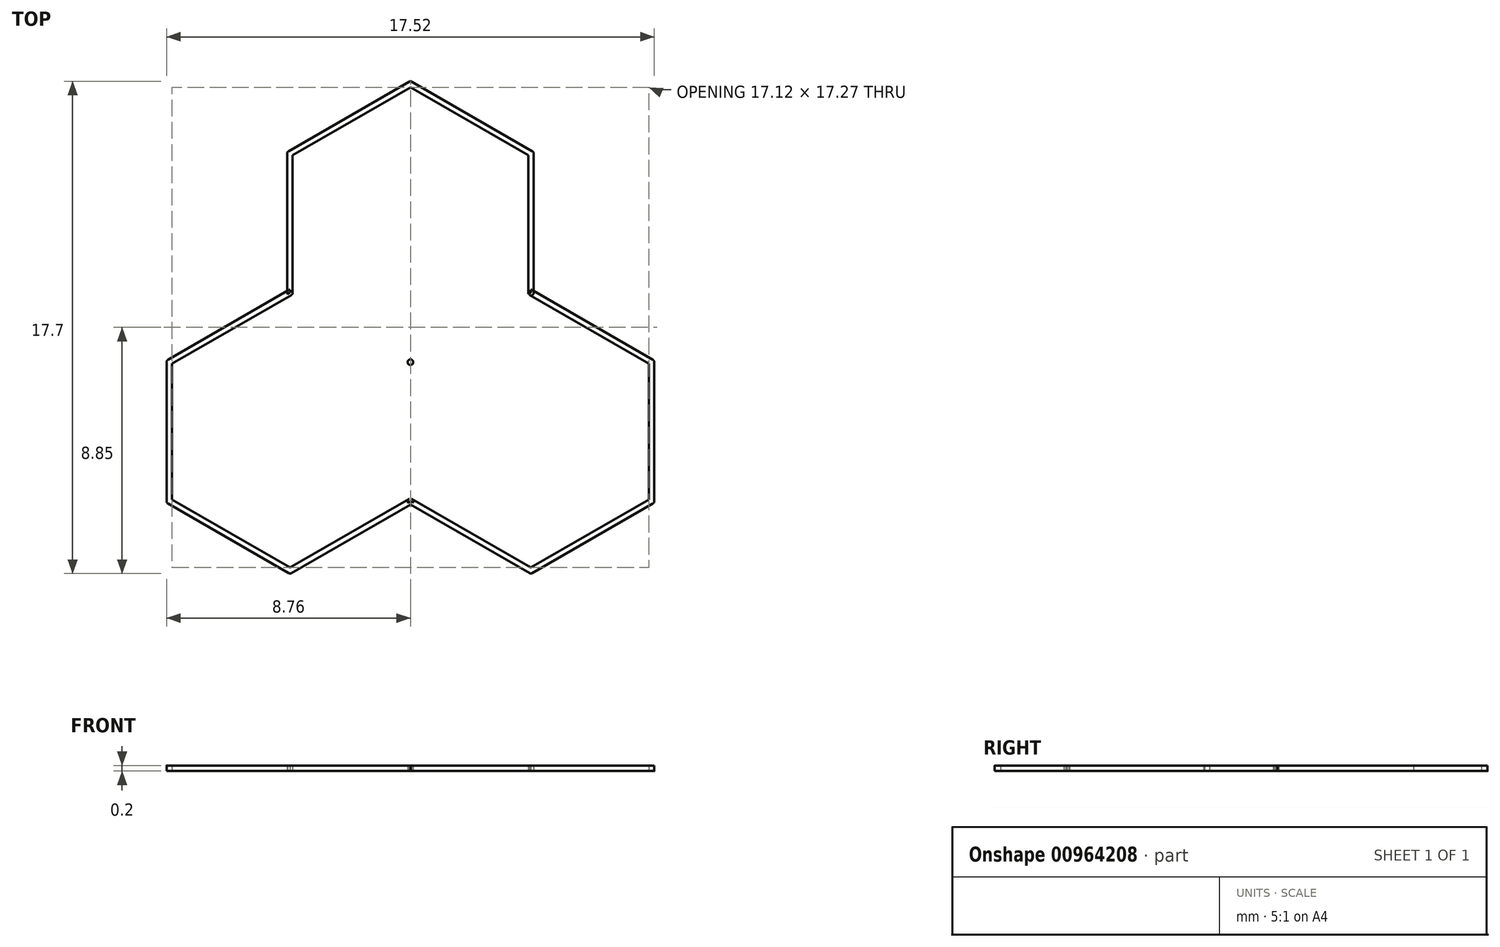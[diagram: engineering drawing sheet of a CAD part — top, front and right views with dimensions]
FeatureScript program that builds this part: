
annotation { "Feature Type Name" : "Feature", "Feature Type Description" : "" }
export const myFeature = defineFeature(function(context is Context, id is Id, definition is map)
    precondition{}
    {
        {
            var Q0;
            Q0=qCreatedBy(makeId("Top.planeOp"),FACE);
            var sketch = newSketch(context, id + "F0", { "sketchPlane" : qUnion([Q0])});
            skLineSegment(sketch, "E0.0", {"start": v(0, 5) * mm, "end": v(4.33, 2.5) * mm});
            skLineSegment(sketch, "E0.1", {"start": v(4.33, 2.5) * mm, "end": v(4.33, -2.5) * mm});
            skLineSegment(sketch, "E0.2", {"start": v(4.33, -2.5) * mm, "end": v(0, -5) * mm});
            skLineSegment(sketch, "E0.3", {"start": v(0, -5) * mm, "end": v(-4.33, -2.5) * mm});
            skLineSegment(sketch, "E0.4", {"start": v(-4.33, -2.5) * mm, "end": v(-4.33, 2.5) * mm});
            skLineSegment(sketch, "E0.5", {"start": v(-4.33, 2.5) * mm, "end": v(0, 5) * mm});
            skLineSegment(sketch, "E1", {"start": v(4.33, -2.5) * mm, "end": v(8.66, -5) * mm});
            skLineSegment(sketch, "E2", {"start": v(8.66, -5) * mm, "end": v(8.66, -10) * mm});
            skLineSegment(sketch, "E3", {"start": v(8.66, -10) * mm, "end": v(4.33, -12.5) * mm});
            skLineSegment(sketch, "E4", {"start": v(4.33, -12.5) * mm, "end": v(0, -10) * mm});
            skLineSegment(sketch, "E5", {"start": v(0, -10) * mm, "end": v(0, -5) * mm});
            skLineSegment(sketch, "E6", {"start": v(0, -10) * mm, "end": v(-4.33, -12.5) * mm});
            skLineSegment(sketch, "E7", {"start": v(-4.33, -12.5) * mm, "end": v(-8.66, -10) * mm});
            skLineSegment(sketch, "E8", {"start": v(-8.66, -10) * mm, "end": v(-8.66, -5) * mm});
            skLineSegment(sketch, "E9", {"start": v(-8.66, -5) * mm, "end": v(-4.33, -2.5) * mm});
            skArc(sketch, "E10.0.startCap", {"start": v(8.61, -9.91) * mm, "mid": v(8.75, -9.95) * mm, "end": v(8.71, -10.09) * mm});
            skArc(sketch, "E10.0.endCap", {"start": v(4.38, -12.59) * mm, "mid": v(4.24, -12.55) * mm, "end": v(4.28, -12.41) * mm});
            skLineSegment(sketch, "E10.0.left", {"start": v(8.71, -10.09) * mm, "end": v(4.38, -12.59) * mm});
            skLineSegment(sketch, "E10.0.right", {"start": v(8.61, -9.91) * mm, "end": v(4.28, -12.41) * mm});
            skArc(sketch, "E10.1.startCap", {"start": v(4.28, -2.59) * mm, "mid": v(4.24, -2.45) * mm, "end": v(4.38, -2.41) * mm});
            skArc(sketch, "E10.1.endCap", {"start": v(8.71, -4.91) * mm, "mid": v(8.75, -5.05) * mm, "end": v(8.61, -5.09) * mm});
            skLineSegment(sketch, "E10.1.left", {"start": v(4.38, -2.41) * mm, "end": v(8.71, -4.91) * mm});
            skLineSegment(sketch, "E10.1.right", {"start": v(4.28, -2.59) * mm, "end": v(8.61, -5.09) * mm});
            skArc(sketch, "E10.2.startCap", {"start": v(8.56, -5) * mm, "mid": v(8.66, -4.9) * mm, "end": v(8.76, -5) * mm});
            skArc(sketch, "E10.2.endCap", {"start": v(8.76, -10) * mm, "mid": v(8.66, -10.1) * mm, "end": v(8.56, -10) * mm});
            skLineSegment(sketch, "E10.2.left", {"start": v(8.76, -5) * mm, "end": v(8.76, -10) * mm});
            skLineSegment(sketch, "E10.2.right", {"start": v(8.56, -5) * mm, "end": v(8.56, -10) * mm});
            skArc(sketch, "E10.3.startCap", {"start": v(-4.28, -12.41) * mm, "mid": v(-4.24, -12.55) * mm, "end": v(-4.38, -12.59) * mm});
            skArc(sketch, "E10.3.endCap", {"start": v(-8.71, -10.09) * mm, "mid": v(-8.75, -9.95) * mm, "end": v(-8.61, -9.91) * mm});
            skLineSegment(sketch, "E10.3.left", {"start": v(-4.38, -12.59) * mm, "end": v(-8.71, -10.09) * mm});
            skLineSegment(sketch, "E10.3.right", {"start": v(-4.28, -12.41) * mm, "end": v(-8.61, -9.91) * mm});
            skArc(sketch, "E10.4.startCap", {"start": v(4.23, 2.5) * mm, "mid": v(4.33, 2.6) * mm, "end": v(4.43, 2.5) * mm});
            skArc(sketch, "E10.4.endCap", {"start": v(4.43, -2.5) * mm, "mid": v(4.33, -2.6) * mm, "end": v(4.23, -2.5) * mm});
            skLineSegment(sketch, "E10.4.left", {"start": v(4.43, 2.5) * mm, "end": v(4.43, -2.5) * mm});
            skLineSegment(sketch, "E10.4.right", {"start": v(4.23, 2.5) * mm, "end": v(4.23, -2.5) * mm});
            skArc(sketch, "E10.5.startCap", {"start": v(-4.28, 2.41) * mm, "mid": v(-4.42, 2.45) * mm, "end": v(-4.38, 2.59) * mm});
            skArc(sketch, "E10.5.endCap", {"start": v(-0.05, 5.09) * mm, "mid": v(0.09, 5.05) * mm, "end": v(0.05, 4.91) * mm});
            skLineSegment(sketch, "E10.5.left", {"start": v(-4.38, 2.59) * mm, "end": v(-0.05, 5.09) * mm});
            skLineSegment(sketch, "E10.5.right", {"start": v(-4.28, 2.41) * mm, "end": v(0.05, 4.91) * mm});
            skArc(sketch, "E10.6.startCap", {"start": v(0.1, -10) * mm, "mid": v(0, -10.1) * mm, "end": v(-0.1, -10) * mm});
            skArc(sketch, "E10.6.endCap", {"start": v(-0.1, -5) * mm, "mid": v(0, -4.9) * mm, "end": v(0.1, -5) * mm});
            skLineSegment(sketch, "E10.6.left", {"start": v(-0.1, -10) * mm, "end": v(-0.1, -5) * mm});
            skLineSegment(sketch, "E10.6.right", {"start": v(0.1, -10) * mm, "end": v(0.1, -5) * mm});
            skArc(sketch, "E10.7.startCap", {"start": v(4.28, -2.41) * mm, "mid": v(4.42, -2.45) * mm, "end": v(4.38, -2.59) * mm});
            skArc(sketch, "E10.7.endCap", {"start": v(0.05, -5.09) * mm, "mid": v(-0.09, -5.05) * mm, "end": v(-0.05, -4.91) * mm});
            skLineSegment(sketch, "E10.7.left", {"start": v(4.38, -2.59) * mm, "end": v(0.05, -5.09) * mm});
            skLineSegment(sketch, "E10.7.right", {"start": v(4.28, -2.41) * mm, "end": v(-0.05, -4.91) * mm});
            skArc(sketch, "E10.8.startCap", {"start": v(4.38, -12.41) * mm, "mid": v(4.42, -12.55) * mm, "end": v(4.28, -12.59) * mm});
            skArc(sketch, "E10.8.endCap", {"start": v(-0.05, -10.09) * mm, "mid": v(-0.09, -9.95) * mm, "end": v(0.05, -9.91) * mm});
            skLineSegment(sketch, "E10.8.left", {"start": v(4.28, -12.59) * mm, "end": v(-0.05, -10.09) * mm});
            skLineSegment(sketch, "E10.8.right", {"start": v(4.38, -12.41) * mm, "end": v(0.05, -9.91) * mm});
            skArc(sketch, "E10.9.startCap", {"start": v(-4.23, -2.5) * mm, "mid": v(-4.33, -2.6) * mm, "end": v(-4.43, -2.5) * mm});
            skArc(sketch, "E10.9.endCap", {"start": v(-4.43, 2.5) * mm, "mid": v(-4.33, 2.6) * mm, "end": v(-4.23, 2.5) * mm});
            skLineSegment(sketch, "E10.9.left", {"start": v(-4.43, -2.5) * mm, "end": v(-4.43, 2.5) * mm});
            skLineSegment(sketch, "E10.9.right", {"start": v(-4.23, -2.5) * mm, "end": v(-4.23, 2.5) * mm});
            skArc(sketch, "E10.10.startCap", {"start": v(-8.56, -10) * mm, "mid": v(-8.66, -10.1) * mm, "end": v(-8.76, -10) * mm});
            skArc(sketch, "E10.10.endCap", {"start": v(-8.76, -5) * mm, "mid": v(-8.66, -4.9) * mm, "end": v(-8.56, -5) * mm});
            skLineSegment(sketch, "E10.10.left", {"start": v(-8.76, -10) * mm, "end": v(-8.76, -5) * mm});
            skLineSegment(sketch, "E10.10.right", {"start": v(-8.56, -10) * mm, "end": v(-8.56, -5) * mm});
            skArc(sketch, "E10.11.startCap", {"start": v(-0.05, -9.91) * mm, "mid": v(0.09, -9.95) * mm, "end": v(0.05, -10.09) * mm});
            skArc(sketch, "E10.11.endCap", {"start": v(-4.28, -12.59) * mm, "mid": v(-4.42, -12.55) * mm, "end": v(-4.38, -12.41) * mm});
            skLineSegment(sketch, "E10.11.left", {"start": v(0.05, -10.09) * mm, "end": v(-4.28, -12.59) * mm});
            skLineSegment(sketch, "E10.11.right", {"start": v(-0.05, -9.91) * mm, "end": v(-4.38, -12.41) * mm});
            skArc(sketch, "E10.12.startCap", {"start": v(-8.61, -5.09) * mm, "mid": v(-8.75, -5.05) * mm, "end": v(-8.71, -4.91) * mm});
            skArc(sketch, "E10.12.endCap", {"start": v(-4.38, -2.41) * mm, "mid": v(-4.24, -2.45) * mm, "end": v(-4.28, -2.59) * mm});
            skLineSegment(sketch, "E10.12.left", {"start": v(-8.71, -4.91) * mm, "end": v(-4.38, -2.41) * mm});
            skLineSegment(sketch, "E10.12.right", {"start": v(-8.61, -5.09) * mm, "end": v(-4.28, -2.59) * mm});
            skArc(sketch, "E10.13.startCap", {"start": v(0.05, -4.91) * mm, "mid": v(0.09, -5.05) * mm, "end": v(-0.05, -5.09) * mm});
            skArc(sketch, "E10.13.endCap", {"start": v(-4.38, -2.59) * mm, "mid": v(-4.42, -2.45) * mm, "end": v(-4.28, -2.41) * mm});
            skLineSegment(sketch, "E10.13.left", {"start": v(-0.05, -5.09) * mm, "end": v(-4.38, -2.59) * mm});
            skLineSegment(sketch, "E10.13.right", {"start": v(0.05, -4.91) * mm, "end": v(-4.28, -2.41) * mm});
            skArc(sketch, "E10.14.startCap", {"start": v(-0.05, 4.91) * mm, "mid": v(-0.09, 5.05) * mm, "end": v(0.05, 5.09) * mm});
            skArc(sketch, "E10.14.endCap", {"start": v(4.38, 2.59) * mm, "mid": v(4.42, 2.45) * mm, "end": v(4.28, 2.41) * mm});
            skLineSegment(sketch, "E10.14.left", {"start": v(0.05, 5.09) * mm, "end": v(4.38, 2.59) * mm});
            skLineSegment(sketch, "E10.14.right", {"start": v(-0.05, 4.91) * mm, "end": v(4.28, 2.41) * mm});
            skSolve(sketch);
        }
        {
            var Q0;
            {var subQ5=sQuery(id+"F0.wireOp",EDGE,"E10.5.left");Q0=makeQuery(id+"F0.imprint","IMPRINT",FACE,{"disambiguationData":[TD([[makeQuery(id+"F0.imprint","IMPRINT",EDGE,{"derivedFrom":subQ5}),-1.0]])]});}
            var Q1;
            {var subQ4=sQuery(id+"F0.wireOp",EDGE,"E0.4");var subQ6=sQuery(id+"F0.wireOp",EDGE,"E0.5");var subQ7=makeQuery(id+"F0.imprint","INTERSECT",VERTEX,{"derivedFrom":[subQ4,subQ6]});Q1=makeQuery(id+"F0.imprint","IMPRINT",FACE,{"disambiguationData":[TD([[makeQuery(id+"F0.imprint","IMPRINT",EDGE,{"disambiguationData":[TD([[subQ7,1.0]])],"derivedFrom":subQ4}),1.0]])]});}
            var Q2;
            {var subQ0=sQuery(id+"F0.wireOp",EDGE,"E0.5");var subQ1=sQuery(id+"F0.wireOp",EDGE,"E0.4");var subQ2=makeQuery(id+"F0.imprint","INTERSECT",VERTEX,{"derivedFrom":[subQ1,subQ0]});Q2=makeQuery(id+"F0.imprint","IMPRINT",FACE,{"disambiguationData":[TD([[makeQuery(id+"F0.imprint","IMPRINT",EDGE,{"disambiguationData":[TD([[subQ2,1.0]])],"derivedFrom":subQ1}),-1.0]])]});}
            var Q3;
            {var subQ5=sQuery(id+"F0.wireOp",EDGE,"E10.13.endCap");var subQ7=sQuery(id+"F0.wireOp",EDGE,"E0.4");var subQ9=makeQuery(id+"F0.imprint","INTERSECT",VERTEX,{"derivedFrom":[subQ7,subQ5]});Q3=makeQuery(id+"F0.imprint","IMPRINT",FACE,{"disambiguationData":[TD([[makeQuery(id+"F0.imprint","IMPRINT",EDGE,{"disambiguationData":[TD([[subQ9,-1.0]])],"derivedFrom":subQ7}),1.0]])]});}
            var Q4;
            {var subQ5=sQuery(id+"F0.wireOp",EDGE,"E10.13.endCap");var subQ7=sQuery(id+"F0.wireOp",EDGE,"E0.4");var subQ8=makeQuery(id+"F0.imprint","INTERSECT",VERTEX,{"derivedFrom":[subQ7,subQ5]});Q4=makeQuery(id+"F0.imprint","IMPRINT",FACE,{"disambiguationData":[TD([[makeQuery(id+"F0.imprint","IMPRINT",EDGE,{"disambiguationData":[TD([[subQ8,-1.0]])],"derivedFrom":subQ7}),-1.0]])]});}
            var Q5;
            {var subQ1=sQuery(id+"F0.wireOp",EDGE,"E10.9.endCap");var subQ5=sQuery(id+"F0.wireOp",EDGE,"E0.5");var subQ6=makeQuery(id+"F0.imprint","INTERSECT",VERTEX,{"derivedFrom":[subQ5,subQ1]});Q5=makeQuery(id+"F0.imprint","IMPRINT",FACE,{"disambiguationData":[TD([[makeQuery(id+"F0.imprint","IMPRINT",EDGE,{"disambiguationData":[TD([[subQ6,-1.0]])],"derivedFrom":subQ5}),-1.0]])]});}
            var Q6;
            {var subQ7=sQuery(id+"F0.wireOp",EDGE,"E0.0");var subQ9=sQuery(id+"F0.wireOp",EDGE,"E0.5");var subQ10=makeQuery(id+"F0.imprint","INTERSECT",VERTEX,{"derivedFrom":[subQ7,subQ9]});Q6=makeQuery(id+"F0.imprint","IMPRINT",FACE,{"disambiguationData":[TD([[makeQuery(id+"F0.imprint","IMPRINT",EDGE,{"disambiguationData":[TD([[subQ10,-1.0]])],"derivedFrom":subQ7}),-1.0]])]});}
            var Q7;
            {var subQ2=sQuery(id+"F0.wireOp",EDGE,"E0.5");var subQ6=sQuery(id+"F0.wireOp",EDGE,"E0.0");var subQ8=makeQuery(id+"F0.imprint","INTERSECT",VERTEX,{"derivedFrom":[subQ6,subQ2]});Q7=makeQuery(id+"F0.imprint","IMPRINT",FACE,{"disambiguationData":[TD([[makeQuery(id+"F0.imprint","IMPRINT",EDGE,{"disambiguationData":[TD([[subQ8,-1.0]])],"derivedFrom":subQ6}),1.0]])]});}
            var Q8;
            {var subQ5=sQuery(id+"F0.wireOp",EDGE,"E10.14.left");Q8=makeQuery(id+"F0.imprint","IMPRINT",FACE,{"disambiguationData":[TD([[makeQuery(id+"F0.imprint","IMPRINT",EDGE,{"derivedFrom":subQ5}),-1.0]])]});}
            var Q9;
            {var subQ1=sQuery(id+"F0.wireOp",EDGE,"E10.5.endCap");var subQ3=sQuery(id+"F0.wireOp",EDGE,"E0.0");var subQ4=makeQuery(id+"F0.imprint","INTERSECT",VERTEX,{"derivedFrom":[subQ3,subQ1]});Q9=makeQuery(id+"F0.imprint","IMPRINT",FACE,{"disambiguationData":[TD([[makeQuery(id+"F0.imprint","IMPRINT",EDGE,{"disambiguationData":[TD([[subQ4,-1.0]])],"derivedFrom":subQ3}),-1.0]])]});}
            var Q10;
            {var subQ5=sQuery(id+"F0.wireOp",EDGE,"E0.0");var subQ7=sQuery(id+"F0.wireOp",EDGE,"E0.1");var subQ8=makeQuery(id+"F0.imprint","INTERSECT",VERTEX,{"derivedFrom":[subQ5,subQ7]});Q10=makeQuery(id+"F0.imprint","IMPRINT",FACE,{"disambiguationData":[TD([[makeQuery(id+"F0.imprint","IMPRINT",EDGE,{"disambiguationData":[TD([[subQ8,1.0]])],"derivedFrom":subQ5}),-1.0]])]});}
            var Q11;
            {var subQ4=sQuery(id+"F0.wireOp",EDGE,"E0.0");var subQ6=sQuery(id+"F0.wireOp",EDGE,"E0.1");var subQ7=makeQuery(id+"F0.imprint","INTERSECT",VERTEX,{"derivedFrom":[subQ4,subQ6]});Q11=makeQuery(id+"F0.imprint","IMPRINT",FACE,{"disambiguationData":[TD([[makeQuery(id+"F0.imprint","IMPRINT",EDGE,{"disambiguationData":[TD([[subQ7,1.0]])],"derivedFrom":subQ4}),1.0]])]});}
            var Q12;
            {var subQ5=sQuery(id+"F0.wireOp",EDGE,"E0.1");var subQ8=sQuery(id+"F0.wireOp",EDGE,"E10.14.endCap");var subQ10=makeQuery(id+"F0.imprint","INTERSECT",VERTEX,{"derivedFrom":[subQ5,subQ8]});Q12=makeQuery(id+"F0.imprint","IMPRINT",FACE,{"disambiguationData":[TD([[makeQuery(id+"F0.imprint","IMPRINT",EDGE,{"disambiguationData":[TD([[subQ10,-1.0]])],"derivedFrom":subQ5}),-1.0]])]});}
            var Q13;
            {var subQ3=sQuery(id+"F0.wireOp",EDGE,"E0.1");var subQ5=sQuery(id+"F0.wireOp",EDGE,"E10.14.endCap");var subQ9=makeQuery(id+"F0.imprint","INTERSECT",VERTEX,{"derivedFrom":[subQ3,subQ5]});Q13=makeQuery(id+"F0.imprint","IMPRINT",FACE,{"disambiguationData":[TD([[makeQuery(id+"F0.imprint","IMPRINT",EDGE,{"disambiguationData":[TD([[subQ9,-1.0]])],"derivedFrom":subQ3}),1.0]])]});}
            var Q14;
            {var subQ0=sQuery(id+"F0.wireOp",EDGE,"E10.1.startCap");Q14=makeQuery(id+"F0.imprint","IMPRINT",FACE,{"disambiguationData":[TD([[makeQuery(id+"F0.imprint","IMPRINT",EDGE,{"derivedFrom":subQ0}),1.0]])]});}
            var Q15;
            {var subQ0=sQuery(id+"F0.wireOp",EDGE,"E10.7.startCap");var subQ1=sQuery(id+"F0.wireOp",EDGE,"E10.1.left");var subQ2=makeQuery(id+"F0.imprint","INTERSECT",VERTEX,{"derivedFrom":[subQ1,subQ0]});Q15=makeQuery(id+"F0.imprint","IMPRINT",FACE,{"disambiguationData":[TD([[makeQuery(id+"F0.imprint","IMPRINT",EDGE,{"disambiguationData":[TD([[subQ2,-1.0]])],"derivedFrom":subQ1}),-1.0]])]});}
            var Q16;
            {var subQ0=sQuery(id+"F0.wireOp",EDGE,"E10.7.startCap");var subQ1=makeQuery(id+"F0.imprint","INTERSECT",VERTEX,{"derivedFrom":[sQuery(id+"F0.wireOp",EDGE,"E10.1.left"),subQ0]});Q16=makeQuery(id+"F0.imprint","IMPRINT",FACE,{"disambiguationData":[TD([[makeQuery(id+"F0.imprint","IMPRINT",EDGE,{"disambiguationData":[TD([[subQ1,1.0]])],"derivedFrom":subQ0}),-1.0]])]});}
            var Q17;
            {var subQ1=sQuery(id+"F0.wireOp",EDGE,"E10.1.startCap");Q17=makeQuery(id+"F0.imprint","IMPRINT",FACE,{"disambiguationData":[TD([[makeQuery(id+"F0.imprint","IMPRINT",EDGE,{"derivedFrom":subQ1}),-1.0]])]});}
            var Q18;
            {var subQ0=sQuery(id+"F0.wireOp",EDGE,"E10.4.endCap");var subQ1=sQuery(id+"F0.wireOp",EDGE,"E10.1.right");var subQ2=makeQuery(id+"F0.imprint","INTERSECT",VERTEX,{"derivedFrom":[subQ1,subQ0]});Q18=makeQuery(id+"F0.imprint","IMPRINT",FACE,{"disambiguationData":[TD([[makeQuery(id+"F0.imprint","IMPRINT",EDGE,{"disambiguationData":[TD([[subQ2,-1.0]])],"derivedFrom":subQ1}),1.0]])]});}
            var Q19;
            {var subQ0=sQuery(id+"F0.wireOp",EDGE,"E10.4.endCap");var subQ1=makeQuery(id+"F0.imprint","INTERSECT",VERTEX,{"derivedFrom":[sQuery(id+"F0.wireOp",EDGE,"E10.1.right"),subQ0]});Q19=makeQuery(id+"F0.imprint","IMPRINT",FACE,{"disambiguationData":[TD([[makeQuery(id+"F0.imprint","IMPRINT",EDGE,{"disambiguationData":[TD([[subQ1,-1.0]])],"derivedFrom":subQ0}),-1.0]])]});}
            var Q20;
            {var subQ1=sQuery(id+"F0.wireOp",EDGE,"E10.4.endCap");var subQ5=sQuery(id+"F0.wireOp",EDGE,"E0.2");var subQ6=makeQuery(id+"F0.imprint","INTERSECT",VERTEX,{"derivedFrom":[subQ5,subQ1]});Q20=makeQuery(id+"F0.imprint","IMPRINT",FACE,{"disambiguationData":[TD([[makeQuery(id+"F0.imprint","IMPRINT",EDGE,{"disambiguationData":[TD([[subQ6,-1.0]])],"derivedFrom":subQ5}),-1.0]])]});}
            var Q21;
            {var subQ5=sQuery(id+"F0.wireOp",EDGE,"E10.4.endCap");var subQ8=sQuery(id+"F0.wireOp",EDGE,"E0.2");var subQ9=makeQuery(id+"F0.imprint","INTERSECT",VERTEX,{"derivedFrom":[subQ8,subQ5]});Q21=makeQuery(id+"F0.imprint","IMPRINT",FACE,{"disambiguationData":[TD([[makeQuery(id+"F0.imprint","IMPRINT",EDGE,{"disambiguationData":[TD([[subQ9,-1.0]])],"derivedFrom":subQ8}),1.0]])]});}
            var Q22;
            {var subQ5=sQuery(id+"F0.wireOp",EDGE,"E1");var subQ9=sQuery(id+"F0.wireOp",EDGE,"E10.7.startCap");var subQ10=makeQuery(id+"F0.imprint","INTERSECT",VERTEX,{"derivedFrom":[subQ5,subQ9]});Q22=makeQuery(id+"F0.imprint","IMPRINT",FACE,{"disambiguationData":[TD([[makeQuery(id+"F0.imprint","IMPRINT",EDGE,{"disambiguationData":[TD([[subQ10,-1.0]])],"derivedFrom":subQ5}),-1.0]])]});}
            var Q23;
            {var subQ0=sQuery(id+"F0.wireOp",EDGE,"E10.7.startCap");var subQ5=sQuery(id+"F0.wireOp",EDGE,"E1");var subQ6=makeQuery(id+"F0.imprint","INTERSECT",VERTEX,{"derivedFrom":[subQ5,subQ0]});Q23=makeQuery(id+"F0.imprint","IMPRINT",FACE,{"disambiguationData":[TD([[makeQuery(id+"F0.imprint","IMPRINT",EDGE,{"disambiguationData":[TD([[subQ6,-1.0]])],"derivedFrom":subQ5}),1.0]])]});}
            var Q24;
            {var subQ0=sQuery(id+"F0.wireOp",EDGE,"E2");var subQ1=sQuery(id+"F0.wireOp",EDGE,"E1");var subQ2=makeQuery(id+"F0.imprint","INTERSECT",VERTEX,{"derivedFrom":[subQ1,subQ0]});Q24=makeQuery(id+"F0.imprint","IMPRINT",FACE,{"disambiguationData":[TD([[makeQuery(id+"F0.imprint","IMPRINT",EDGE,{"disambiguationData":[TD([[subQ2,1.0]])],"derivedFrom":subQ1}),-1.0]])]});}
            var Q25;
            {var subQ2=sQuery(id+"F0.wireOp",EDGE,"E1");var subQ6=sQuery(id+"F0.wireOp",EDGE,"E2");var subQ8=makeQuery(id+"F0.imprint","INTERSECT",VERTEX,{"derivedFrom":[subQ2,subQ6]});Q25=makeQuery(id+"F0.imprint","IMPRINT",FACE,{"disambiguationData":[TD([[makeQuery(id+"F0.imprint","IMPRINT",EDGE,{"disambiguationData":[TD([[subQ8,1.0]])],"derivedFrom":subQ2}),1.0]])]});}
            var Q26;
            {var subQ5=sQuery(id+"F0.wireOp",EDGE,"E10.2.left");Q26=makeQuery(id+"F0.imprint","IMPRINT",FACE,{"disambiguationData":[TD([[makeQuery(id+"F0.imprint","IMPRINT",EDGE,{"derivedFrom":subQ5}),-1.0]])]});}
            var Q27;
            {var subQ1=sQuery(id+"F0.wireOp",EDGE,"E10.1.endCap");var subQ3=sQuery(id+"F0.wireOp",EDGE,"E2");var subQ4=makeQuery(id+"F0.imprint","INTERSECT",VERTEX,{"derivedFrom":[subQ3,subQ1]});Q27=makeQuery(id+"F0.imprint","IMPRINT",FACE,{"disambiguationData":[TD([[makeQuery(id+"F0.imprint","IMPRINT",EDGE,{"disambiguationData":[TD([[subQ4,-1.0]])],"derivedFrom":subQ3}),-1.0]])]});}
            var Q28;
            {var subQ5=sQuery(id+"F0.wireOp",EDGE,"E2");var subQ7=sQuery(id+"F0.wireOp",EDGE,"E3");var subQ8=makeQuery(id+"F0.imprint","INTERSECT",VERTEX,{"derivedFrom":[subQ5,subQ7]});Q28=makeQuery(id+"F0.imprint","IMPRINT",FACE,{"disambiguationData":[TD([[makeQuery(id+"F0.imprint","IMPRINT",EDGE,{"disambiguationData":[TD([[subQ8,1.0]])],"derivedFrom":subQ5}),-1.0]])]});}
            var Q29;
            {var subQ3=sQuery(id+"F0.wireOp",EDGE,"E2");var subQ5=sQuery(id+"F0.wireOp",EDGE,"E3");var subQ6=makeQuery(id+"F0.imprint","INTERSECT",VERTEX,{"derivedFrom":[subQ3,subQ5]});Q29=makeQuery(id+"F0.imprint","IMPRINT",FACE,{"disambiguationData":[TD([[makeQuery(id+"F0.imprint","IMPRINT",EDGE,{"disambiguationData":[TD([[subQ6,1.0]])],"derivedFrom":subQ3}),1.0]])]});}
            var Q30;
            {var subQ5=sQuery(id+"F0.wireOp",EDGE,"E10.0.left");Q30=makeQuery(id+"F0.imprint","IMPRINT",FACE,{"disambiguationData":[TD([[makeQuery(id+"F0.imprint","IMPRINT",EDGE,{"derivedFrom":subQ5}),-1.0]])]});}
            var Q31;
            {var subQ1=sQuery(id+"F0.wireOp",EDGE,"E10.2.endCap");var subQ3=sQuery(id+"F0.wireOp",EDGE,"E3");var subQ4=makeQuery(id+"F0.imprint","INTERSECT",VERTEX,{"derivedFrom":[subQ3,subQ1]});Q31=makeQuery(id+"F0.imprint","IMPRINT",FACE,{"disambiguationData":[TD([[makeQuery(id+"F0.imprint","IMPRINT",EDGE,{"disambiguationData":[TD([[subQ4,-1.0]])],"derivedFrom":subQ3}),-1.0]])]});}
            var Q32;
            {var subQ2=sQuery(id+"F0.wireOp",EDGE,"E3");var subQ6=sQuery(id+"F0.wireOp",EDGE,"E4");var subQ8=makeQuery(id+"F0.imprint","INTERSECT",VERTEX,{"derivedFrom":[subQ2,subQ6]});Q32=makeQuery(id+"F0.imprint","IMPRINT",FACE,{"disambiguationData":[TD([[makeQuery(id+"F0.imprint","IMPRINT",EDGE,{"disambiguationData":[TD([[subQ8,1.0]])],"derivedFrom":subQ2}),1.0]])]});}
            var Q33;
            {var subQ3=sQuery(id+"F0.wireOp",EDGE,"E4");var subQ5=sQuery(id+"F0.wireOp",EDGE,"E3");var subQ6=makeQuery(id+"F0.imprint","INTERSECT",VERTEX,{"derivedFrom":[subQ5,subQ3]});Q33=makeQuery(id+"F0.imprint","IMPRINT",FACE,{"disambiguationData":[TD([[makeQuery(id+"F0.imprint","IMPRINT",EDGE,{"disambiguationData":[TD([[subQ6,1.0]])],"derivedFrom":subQ5}),-1.0]])]});}
            var Q34;
            {var subQ6=sQuery(id+"F0.wireOp",EDGE,"E10.0.endCap");var subQ9=sQuery(id+"F0.wireOp",EDGE,"E4");var subQ11=makeQuery(id+"F0.imprint","INTERSECT",VERTEX,{"derivedFrom":[subQ9,subQ6]});Q34=makeQuery(id+"F0.imprint","IMPRINT",FACE,{"disambiguationData":[TD([[makeQuery(id+"F0.imprint","IMPRINT",EDGE,{"disambiguationData":[TD([[subQ11,-1.0]])],"derivedFrom":subQ9}),-1.0]])]});}
            var Q35;
            {var subQ1=sQuery(id+"F0.wireOp",EDGE,"E10.0.endCap");var subQ7=sQuery(id+"F0.wireOp",EDGE,"E4");var subQ9=makeQuery(id+"F0.imprint","INTERSECT",VERTEX,{"derivedFrom":[subQ7,subQ1]});Q35=makeQuery(id+"F0.imprint","IMPRINT",FACE,{"disambiguationData":[TD([[makeQuery(id+"F0.imprint","IMPRINT",EDGE,{"disambiguationData":[TD([[subQ9,-1.0]])],"derivedFrom":subQ7}),1.0]])]});}
            var Q36;
            {var subQ0=sQuery(id+"F0.wireOp",EDGE,"E10.6.endCap");Q36=makeQuery(id+"F0.imprint","IMPRINT",FACE,{"disambiguationData":[TD([[makeQuery(id+"F0.imprint","IMPRINT",EDGE,{"derivedFrom":subQ0}),1.0]])]});}
            var Q37;
            {var subQ0=sQuery(id+"F0.wireOp",EDGE,"E10.7.endCap");var subQ1=sQuery(id+"F0.wireOp",EDGE,"E10.6.left");var subQ2=makeQuery(id+"F0.imprint","INTERSECT",VERTEX,{"derivedFrom":[subQ1,subQ0]});Q37=makeQuery(id+"F0.imprint","IMPRINT",FACE,{"disambiguationData":[TD([[makeQuery(id+"F0.imprint","IMPRINT",EDGE,{"disambiguationData":[TD([[subQ2,1.0]])],"derivedFrom":subQ1}),-1.0]])]});}
            var Q38;
            {var subQ0=sQuery(id+"F0.wireOp",EDGE,"E10.13.startCap");var subQ1=sQuery(id+"F0.wireOp",EDGE,"E10.6.right");var subQ2=makeQuery(id+"F0.imprint","INTERSECT",VERTEX,{"derivedFrom":[subQ1,subQ0]});Q38=makeQuery(id+"F0.imprint","IMPRINT",FACE,{"disambiguationData":[TD([[makeQuery(id+"F0.imprint","IMPRINT",EDGE,{"disambiguationData":[TD([[subQ2,1.0]])],"derivedFrom":subQ1}),1.0]])]});}
            var Q39;
            {var subQ0=sQuery(id+"F0.wireOp",EDGE,"E10.13.startCap");var subQ1=makeQuery(id+"F0.imprint","INTERSECT",VERTEX,{"derivedFrom":[sQuery(id+"F0.wireOp",EDGE,"E10.6.right"),subQ0]});Q39=makeQuery(id+"F0.imprint","IMPRINT",FACE,{"disambiguationData":[TD([[makeQuery(id+"F0.imprint","IMPRINT",EDGE,{"disambiguationData":[TD([[subQ1,1.0]])],"derivedFrom":subQ0}),-1.0]])]});}
            var Q40;
            {var subQ0=sQuery(id+"F0.wireOp",EDGE,"E10.7.endCap");var subQ1=makeQuery(id+"F0.imprint","INTERSECT",VERTEX,{"derivedFrom":[sQuery(id+"F0.wireOp",EDGE,"E10.6.left"),subQ0]});Q40=makeQuery(id+"F0.imprint","IMPRINT",FACE,{"disambiguationData":[TD([[makeQuery(id+"F0.imprint","IMPRINT",EDGE,{"disambiguationData":[TD([[subQ1,-1.0]])],"derivedFrom":subQ0}),-1.0]])]});}
            var Q41;
            {var subQ1=sQuery(id+"F0.wireOp",EDGE,"E10.6.endCap");Q41=makeQuery(id+"F0.imprint","IMPRINT",FACE,{"disambiguationData":[TD([[makeQuery(id+"F0.imprint","IMPRINT",EDGE,{"derivedFrom":subQ1}),-1.0]])]});}
            var Q42;
            {var subQ0=sQuery(id+"F0.wireOp",EDGE,"E10.11.startCap");var subQ9=sQuery(id+"F0.wireOp",EDGE,"E5");var subQ10=makeQuery(id+"F0.imprint","INTERSECT",VERTEX,{"derivedFrom":[subQ9,subQ0]});Q42=makeQuery(id+"F0.imprint","IMPRINT",FACE,{"disambiguationData":[TD([[makeQuery(id+"F0.imprint","IMPRINT",EDGE,{"disambiguationData":[TD([[subQ10,-1.0]])],"derivedFrom":subQ9}),-1.0]])]});}
            var Q43;
            {var subQ1=sQuery(id+"F0.wireOp",EDGE,"E10.11.startCap");var subQ5=sQuery(id+"F0.wireOp",EDGE,"E5");var subQ6=makeQuery(id+"F0.imprint","INTERSECT",VERTEX,{"derivedFrom":[subQ5,subQ1]});Q43=makeQuery(id+"F0.imprint","IMPRINT",FACE,{"disambiguationData":[TD([[makeQuery(id+"F0.imprint","IMPRINT",EDGE,{"disambiguationData":[TD([[subQ6,-1.0]])],"derivedFrom":subQ5}),1.0]])]});}
            var Q44;
            {var subQ6=sQuery(id+"F0.wireOp",EDGE,"E10.7.endCap");var subQ9=sQuery(id+"F0.wireOp",EDGE,"E0.3");var subQ10=makeQuery(id+"F0.imprint","INTERSECT",VERTEX,{"derivedFrom":[subQ9,subQ6]});Q44=makeQuery(id+"F0.imprint","IMPRINT",FACE,{"disambiguationData":[TD([[makeQuery(id+"F0.imprint","IMPRINT",EDGE,{"disambiguationData":[TD([[subQ10,-1.0]])],"derivedFrom":subQ9}),-1.0]])]});}
            var Q45;
            {var subQ3=sQuery(id+"F0.wireOp",EDGE,"E0.3");var subQ5=sQuery(id+"F0.wireOp",EDGE,"E10.7.endCap");var subQ8=makeQuery(id+"F0.imprint","INTERSECT",VERTEX,{"derivedFrom":[subQ3,subQ5]});Q45=makeQuery(id+"F0.imprint","IMPRINT",FACE,{"disambiguationData":[TD([[makeQuery(id+"F0.imprint","IMPRINT",EDGE,{"disambiguationData":[TD([[subQ8,-1.0]])],"derivedFrom":subQ3}),1.0]])]});}
            var Q46;
            {var subQ0=sQuery(id+"F0.wireOp",EDGE,"E10.11.startCap");var subQ1=sQuery(id+"F0.wireOp",EDGE,"E10.6.right");var subQ2=makeQuery(id+"F0.imprint","INTERSECT",VERTEX,{"derivedFrom":[subQ1,subQ0]});Q46=makeQuery(id+"F0.imprint","IMPRINT",FACE,{"disambiguationData":[TD([[makeQuery(id+"F0.imprint","IMPRINT",EDGE,{"disambiguationData":[TD([[subQ2,-1.0]])],"derivedFrom":subQ1}),1.0]])]});}
            var Q47;
            {var subQ0=sQuery(id+"F0.wireOp",EDGE,"E10.8.endCap");var subQ1=sQuery(id+"F0.wireOp",EDGE,"E10.6.left");var subQ2=makeQuery(id+"F0.imprint","INTERSECT",VERTEX,{"derivedFrom":[subQ1,subQ0]});Q47=makeQuery(id+"F0.imprint","IMPRINT",FACE,{"disambiguationData":[TD([[makeQuery(id+"F0.imprint","IMPRINT",EDGE,{"disambiguationData":[TD([[subQ2,-1.0]])],"derivedFrom":subQ1}),-1.0]])]});}
            var Q48;
            {var subQ0=sQuery(id+"F0.wireOp",EDGE,"E10.6.startCap");Q48=makeQuery(id+"F0.imprint","IMPRINT",FACE,{"disambiguationData":[TD([[makeQuery(id+"F0.imprint","IMPRINT",EDGE,{"derivedFrom":subQ0}),1.0]])]});}
            var Q49;
            {var subQ1=sQuery(id+"F0.wireOp",EDGE,"E10.8.endCap");var subQ5=sQuery(id+"F0.wireOp",EDGE,"E6");var subQ6=makeQuery(id+"F0.imprint","INTERSECT",VERTEX,{"derivedFrom":[subQ5,subQ1]});Q49=makeQuery(id+"F0.imprint","IMPRINT",FACE,{"disambiguationData":[TD([[makeQuery(id+"F0.imprint","IMPRINT",EDGE,{"disambiguationData":[TD([[subQ6,-1.0]])],"derivedFrom":subQ5}),1.0]])]});}
            var Q50;
            {var subQ5=sQuery(id+"F0.wireOp",EDGE,"E6");var subQ9=sQuery(id+"F0.wireOp",EDGE,"E10.8.endCap");var subQ11=makeQuery(id+"F0.imprint","INTERSECT",VERTEX,{"derivedFrom":[subQ5,subQ9]});Q50=makeQuery(id+"F0.imprint","IMPRINT",FACE,{"disambiguationData":[TD([[makeQuery(id+"F0.imprint","IMPRINT",EDGE,{"disambiguationData":[TD([[subQ11,-1.0]])],"derivedFrom":subQ5}),-1.0]])]});}
            var Q51;
            {var subQ0=sQuery(id+"F0.wireOp",EDGE,"E10.8.endCap");var subQ1=makeQuery(id+"F0.imprint","INTERSECT",VERTEX,{"derivedFrom":[sQuery(id+"F0.wireOp",EDGE,"E10.6.left"),subQ0]});Q51=makeQuery(id+"F0.imprint","IMPRINT",FACE,{"disambiguationData":[TD([[makeQuery(id+"F0.imprint","IMPRINT",EDGE,{"disambiguationData":[TD([[subQ1,1.0]])],"derivedFrom":subQ0}),-1.0]])]});}
            var Q52;
            {var subQ0=sQuery(id+"F0.wireOp",EDGE,"E10.11.startCap");var subQ2=makeQuery(id+"F0.imprint","INTERSECT",VERTEX,{"derivedFrom":[sQuery(id+"F0.wireOp",EDGE,"E10.8.right"),subQ0]});Q52=makeQuery(id+"F0.imprint","IMPRINT",FACE,{"disambiguationData":[TD([[makeQuery(id+"F0.imprint","IMPRINT",EDGE,{"disambiguationData":[TD([[subQ2,1.0]])],"derivedFrom":subQ0}),-1.0]])]});}
            var Q53;
            {var subQ1=sQuery(id+"F0.wireOp",EDGE,"E10.6.startCap");Q53=makeQuery(id+"F0.imprint","IMPRINT",FACE,{"disambiguationData":[TD([[makeQuery(id+"F0.imprint","IMPRINT",EDGE,{"derivedFrom":subQ1}),-1.0]])]});}
            var Q54;
            {var subQ5=sQuery(id+"F0.wireOp",EDGE,"E6");var subQ7=sQuery(id+"F0.wireOp",EDGE,"E7");var subQ8=makeQuery(id+"F0.imprint","INTERSECT",VERTEX,{"derivedFrom":[subQ5,subQ7]});Q54=makeQuery(id+"F0.imprint","IMPRINT",FACE,{"disambiguationData":[TD([[makeQuery(id+"F0.imprint","IMPRINT",EDGE,{"disambiguationData":[TD([[subQ8,1.0]])],"derivedFrom":subQ5}),-1.0]])]});}
            var Q55;
            {var subQ4=sQuery(id+"F0.wireOp",EDGE,"E6");var subQ6=sQuery(id+"F0.wireOp",EDGE,"E7");var subQ7=makeQuery(id+"F0.imprint","INTERSECT",VERTEX,{"derivedFrom":[subQ4,subQ6]});Q55=makeQuery(id+"F0.imprint","IMPRINT",FACE,{"disambiguationData":[TD([[makeQuery(id+"F0.imprint","IMPRINT",EDGE,{"disambiguationData":[TD([[subQ7,1.0]])],"derivedFrom":subQ4}),1.0]])]});}
            var Q56;
            {var subQ5=sQuery(id+"F0.wireOp",EDGE,"E10.3.left");Q56=makeQuery(id+"F0.imprint","IMPRINT",FACE,{"disambiguationData":[TD([[makeQuery(id+"F0.imprint","IMPRINT",EDGE,{"derivedFrom":subQ5}),-1.0]])]});}
            var Q57;
            {var subQ5=sQuery(id+"F0.wireOp",EDGE,"E7");var subQ9=sQuery(id+"F0.wireOp",EDGE,"E10.11.endCap");var subQ10=makeQuery(id+"F0.imprint","INTERSECT",VERTEX,{"derivedFrom":[subQ5,subQ9]});Q57=makeQuery(id+"F0.imprint","IMPRINT",FACE,{"disambiguationData":[TD([[makeQuery(id+"F0.imprint","IMPRINT",EDGE,{"disambiguationData":[TD([[subQ10,-1.0]])],"derivedFrom":subQ5}),-1.0]])]});}
            var Q58;
            {var subQ3=sQuery(id+"F0.wireOp",EDGE,"E8");var subQ5=sQuery(id+"F0.wireOp",EDGE,"E7");var subQ6=makeQuery(id+"F0.imprint","INTERSECT",VERTEX,{"derivedFrom":[subQ5,subQ3]});Q58=makeQuery(id+"F0.imprint","IMPRINT",FACE,{"disambiguationData":[TD([[makeQuery(id+"F0.imprint","IMPRINT",EDGE,{"disambiguationData":[TD([[subQ6,1.0]])],"derivedFrom":subQ5}),-1.0]])]});}
            var Q59;
            {var subQ2=sQuery(id+"F0.wireOp",EDGE,"E7");var subQ4=sQuery(id+"F0.wireOp",EDGE,"E8");var subQ5=makeQuery(id+"F0.imprint","INTERSECT",VERTEX,{"derivedFrom":[subQ2,subQ4]});Q59=makeQuery(id+"F0.imprint","IMPRINT",FACE,{"disambiguationData":[TD([[makeQuery(id+"F0.imprint","IMPRINT",EDGE,{"disambiguationData":[TD([[subQ5,1.0]])],"derivedFrom":subQ2}),1.0]])]});}
            var Q60;
            {var subQ5=sQuery(id+"F0.wireOp",EDGE,"E10.10.left");Q60=makeQuery(id+"F0.imprint","IMPRINT",FACE,{"disambiguationData":[TD([[makeQuery(id+"F0.imprint","IMPRINT",EDGE,{"derivedFrom":subQ5}),-1.0]])]});}
            var Q61;
            {var subQ5=sQuery(id+"F0.wireOp",EDGE,"E10.3.endCap");var subQ7=sQuery(id+"F0.wireOp",EDGE,"E8");var subQ8=makeQuery(id+"F0.imprint","INTERSECT",VERTEX,{"derivedFrom":[subQ7,subQ5]});Q61=makeQuery(id+"F0.imprint","IMPRINT",FACE,{"disambiguationData":[TD([[makeQuery(id+"F0.imprint","IMPRINT",EDGE,{"disambiguationData":[TD([[subQ8,-1.0]])],"derivedFrom":subQ7}),-1.0]])]});}
            var Q62;
            {var subQ3=sQuery(id+"F0.wireOp",EDGE,"E9");var subQ9=sQuery(id+"F0.wireOp",EDGE,"E8");var subQ10=makeQuery(id+"F0.imprint","INTERSECT",VERTEX,{"derivedFrom":[subQ9,subQ3]});Q62=makeQuery(id+"F0.imprint","IMPRINT",FACE,{"disambiguationData":[TD([[makeQuery(id+"F0.imprint","IMPRINT",EDGE,{"disambiguationData":[TD([[subQ10,1.0]])],"derivedFrom":subQ9}),-1.0]])]});}
            var Q63;
            {var subQ2=sQuery(id+"F0.wireOp",EDGE,"E8");var subQ4=sQuery(id+"F0.wireOp",EDGE,"E9");var subQ5=makeQuery(id+"F0.imprint","INTERSECT",VERTEX,{"derivedFrom":[subQ2,subQ4]});Q63=makeQuery(id+"F0.imprint","IMPRINT",FACE,{"disambiguationData":[TD([[makeQuery(id+"F0.imprint","IMPRINT",EDGE,{"disambiguationData":[TD([[subQ5,1.0]])],"derivedFrom":subQ2}),1.0]])]});}
            var Q64;
            {var subQ1=sQuery(id+"F0.wireOp",EDGE,"E10.10.endCap");var subQ7=sQuery(id+"F0.wireOp",EDGE,"E9");var subQ9=makeQuery(id+"F0.imprint","INTERSECT",VERTEX,{"derivedFrom":[subQ7,subQ1]});Q64=makeQuery(id+"F0.imprint","IMPRINT",FACE,{"disambiguationData":[TD([[makeQuery(id+"F0.imprint","IMPRINT",EDGE,{"disambiguationData":[TD([[subQ9,-1.0]])],"derivedFrom":subQ7}),1.0]])]});}
            var Q65;
            {var subQ5=sQuery(id+"F0.wireOp",EDGE,"E10.10.endCap");var subQ7=sQuery(id+"F0.wireOp",EDGE,"E9");var subQ8=makeQuery(id+"F0.imprint","INTERSECT",VERTEX,{"derivedFrom":[subQ7,subQ5]});Q65=makeQuery(id+"F0.imprint","IMPRINT",FACE,{"disambiguationData":[TD([[makeQuery(id+"F0.imprint","IMPRINT",EDGE,{"disambiguationData":[TD([[subQ8,-1.0]])],"derivedFrom":subQ7}),-1.0]])]});}
            var Q66;
            {var subQ0=sQuery(id+"F0.wireOp",EDGE,"E10.13.endCap");var subQ1=sQuery(id+"F0.wireOp",EDGE,"E10.9.left");var subQ2=makeQuery(id+"F0.imprint","INTERSECT",VERTEX,{"derivedFrom":[subQ1,subQ0]});Q66=makeQuery(id+"F0.imprint","IMPRINT",FACE,{"disambiguationData":[TD([[makeQuery(id+"F0.imprint","IMPRINT",EDGE,{"disambiguationData":[TD([[subQ2,-1.0]])],"derivedFrom":subQ1}),-1.0]])]});}
            var Q67;
            {var subQ0=sQuery(id+"F0.wireOp",EDGE,"E10.12.endCap");var subQ1=sQuery(id+"F0.wireOp",EDGE,"E10.9.right");var subQ2=makeQuery(id+"F0.imprint","INTERSECT",VERTEX,{"derivedFrom":[subQ1,subQ0]});Q67=makeQuery(id+"F0.imprint","IMPRINT",FACE,{"disambiguationData":[TD([[makeQuery(id+"F0.imprint","IMPRINT",EDGE,{"disambiguationData":[TD([[subQ2,-1.0]])],"derivedFrom":subQ1}),1.0]])]});}
            var Q68;
            {var subQ0=sQuery(id+"F0.wireOp",EDGE,"E10.13.endCap");var subQ1=makeQuery(id+"F0.imprint","INTERSECT",VERTEX,{"derivedFrom":[sQuery(id+"F0.wireOp",EDGE,"E10.9.left"),subQ0]});Q68=makeQuery(id+"F0.imprint","IMPRINT",FACE,{"disambiguationData":[TD([[makeQuery(id+"F0.imprint","IMPRINT",EDGE,{"disambiguationData":[TD([[subQ1,1.0]])],"derivedFrom":subQ0}),-1.0]])]});}
            var Q69;
            {var subQ0=sQuery(id+"F0.wireOp",EDGE,"E10.9.startCap");Q69=makeQuery(id+"F0.imprint","IMPRINT",FACE,{"disambiguationData":[TD([[makeQuery(id+"F0.imprint","IMPRINT",EDGE,{"derivedFrom":subQ0}),1.0]])]});}
            var Q70;
            {var subQ0=sQuery(id+"F0.wireOp",EDGE,"E10.9.startCap");Q70=makeQuery(id+"F0.imprint","IMPRINT",FACE,{"disambiguationData":[TD([[makeQuery(id+"F0.imprint","IMPRINT",EDGE,{"derivedFrom":subQ0}),-1.0]])]});}
            var Q71;
            {var subQ0=sQuery(id+"F0.wireOp",EDGE,"E10.12.endCap");var subQ1=makeQuery(id+"F0.imprint","INTERSECT",VERTEX,{"derivedFrom":[sQuery(id+"F0.wireOp",EDGE,"E10.9.right"),subQ0]});Q71=makeQuery(id+"F0.imprint","IMPRINT",FACE,{"disambiguationData":[TD([[makeQuery(id+"F0.imprint","IMPRINT",EDGE,{"disambiguationData":[TD([[subQ1,-1.0]])],"derivedFrom":subQ0}),-1.0]])]});}
            extrude(context, id + "F1", {"entities" : qUnion([Q0, Q1, Q2, Q3, Q4, Q5, Q6, Q7, Q8, Q9, Q10, Q11, Q12, Q13, Q14, Q15, Q16, Q17, Q18, Q19, Q20, Q21, Q22, Q23, Q24, Q25, Q26, Q27, Q28, Q29, Q30, Q31, Q32, Q33, Q34, Q35, Q36, Q37, Q38, Q39, Q40, Q41, Q42, Q43, Q44, Q45, Q46, Q47, Q48, Q49, Q50, Q51, Q52, Q53, Q54, Q55, Q56, Q57, Q58, Q59, Q60, Q61, Q62, Q63, Q64, Q65, Q66, Q67, Q68, Q69, Q70, Q71]), "depth" : .2 * mm, "offsetDistance" : 25 * mm});
        }
    });
